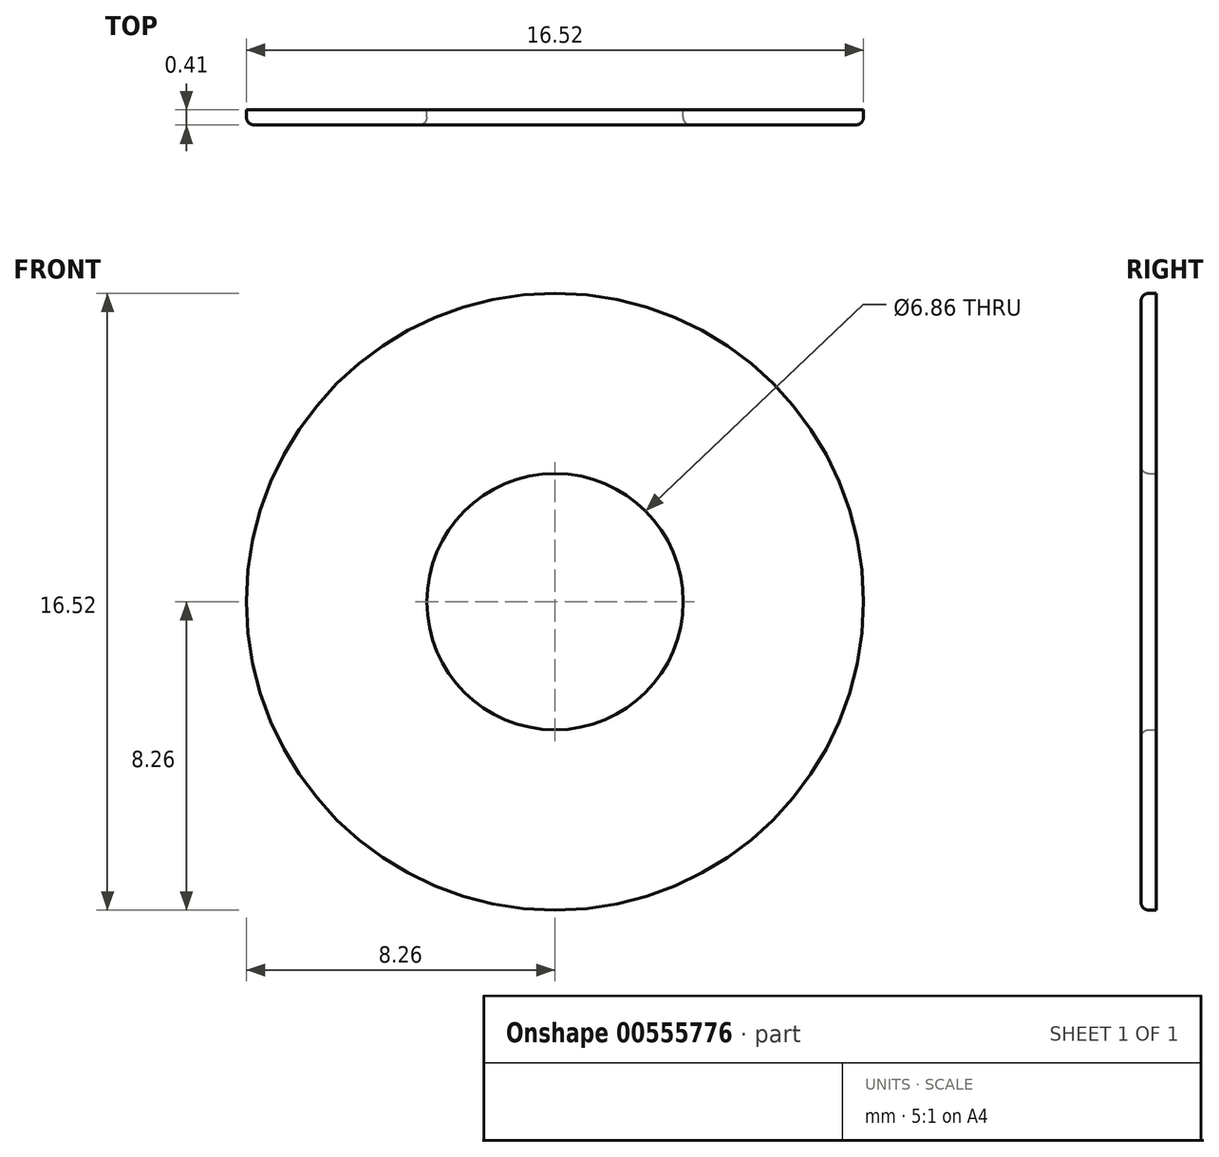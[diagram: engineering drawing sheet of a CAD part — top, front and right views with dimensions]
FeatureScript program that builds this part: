
annotation { "Feature Type Name" : "Feature", "Feature Type Description" : "" }
export const myFeature = defineFeature(function(context is Context, id is Id, definition is map)
    precondition{}
    {
        {
            var Q0;
            Q0=qCreatedBy(makeId("Front.planeOp"),FACE);
            var sketch = newSketch(context, id + "F0", { "sketchPlane" : qUnion([Q0])});
            skCircle(sketch, "E0", {"center": v(0, 0) * mm, "radius": 3.43 * mm});
            skCircle(sketch, "E1", {"center": v(0, 0) * mm, "radius": 8.26 * mm});
            skSolve(sketch);
        }
        {
            var Q0;
            Q0=makeQuery(id+"F0.imprint","IMPRINT",FACE,{"disambiguationData":[TD([[makeQuery(id+"F0.imprint","IMPRINT",EDGE,{"derivedFrom":sQuery(id+"F0.wireOp",EDGE,"E0")}),-1.0]])]});
            extrude(context, id + "F1", {"entities" : qUnion([Q0]), "depth" : 0.4 * mm, "offsetDistance" : 25.4 * mm});
        }
        {
            var Q0;
            Q0=makeQuery(id+"F1.opExtrude","CAP_EDGE",EDGE,{"disambiguationData":[OSD([sQuery(id+"F0.wireOp",EDGE,"E0")])],"isStart":false});
            var Q1;
            Q1=makeQuery(id+"F1.opExtrude","CAP_EDGE",EDGE,{"disambiguationData":[OSD([sQuery(id+"F0.wireOp",EDGE,"E1")])],"isStart":false});
            fillet(context, id + "F2", {"entities" : qUnion([Q0, Q1]), "radius" : 0.2 * mm, "tangentPropagation" : true, "allowEdgeOverflow" : false});
        }
    });
